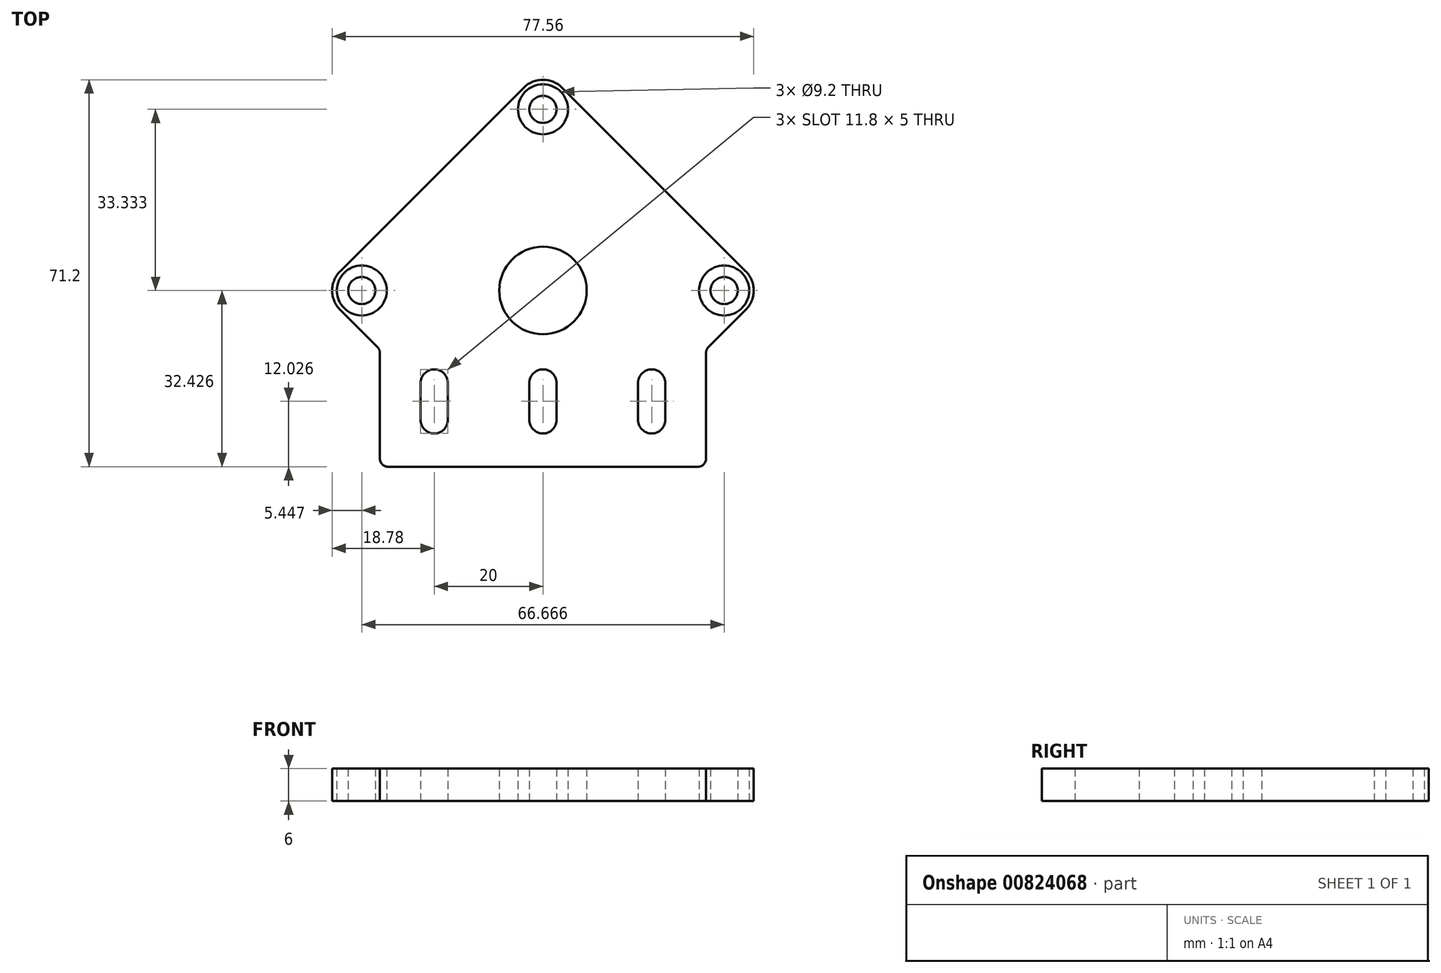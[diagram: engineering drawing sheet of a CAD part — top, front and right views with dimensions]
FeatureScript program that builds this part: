
annotation { "Feature Type Name" : "Feature", "Feature Type Description" : "" }
export const myFeature = defineFeature(function(context is Context, id is Id, definition is map)
    precondition{}
    {
        {
            var Q0;
            Q0=qCreatedBy(makeId("Top.planeOp"),FACE);
            var sketch = newSketch(context, id + "F0", { "sketchPlane" : qUnion([Q0])});
            skLineSegment(sketch, "E0", {"start": v(-28.5, -35.6) * mm, "end": v(28.5, -35.6) * mm});
            skLineSegment(sketch, "E1", {"start": v(-37.31, -6.7) * mm, "end": v(-30.44, -13.58) * mm});
            skLineSegment(sketch, "E2", {"start": v(-30, -14.65) * mm, "end": v(-30, -34.1) * mm});
            skLineSegment(sketch, "E3", {"start": v(-3.54, 34.14) * mm, "end": v(-37.31, 0.36) * mm});
            skLineSegment(sketch, "E4", {"start": v(-22.5, -26.97) * mm, "end": v(-22.5, -20.17) * mm});
            skLineSegment(sketch, "E5", {"start": v(-17.5, -20.17) * mm, "end": v(-17.5, -26.97) * mm});
            skLineSegment(sketch, "E6", {"start": v(-2.5, -26.97) * mm, "end": v(-2.5, -20.17) * mm});
            skLineSegment(sketch, "E7", {"start": v(2.5, -20.17) * mm, "end": v(2.5, -26.97) * mm});
            skLineSegment(sketch, "E8", {"start": v(17.5, -26.97) * mm, "end": v(17.5, -20.17) * mm});
            skLineSegment(sketch, "E9", {"start": v(22.5, -20.17) * mm, "end": v(22.5, -26.97) * mm});
            skLineSegment(sketch, "E10", {"start": v(37.31, 0.36) * mm, "end": v(3.54, 34.14) * mm});
            skLineSegment(sketch, "E11", {"start": v(30, -34.1) * mm, "end": v(30, -14.65) * mm});
            skLineSegment(sketch, "E12", {"start": v(30.44, -13.58) * mm, "end": v(37.31, -6.7) * mm});
            skCircle(sketch, "E13", {"center": v(0, -3.17) * mm, "radius": 8.05 * mm});
            skCircle(sketch, "E14", {"center": v(0, -3.17) * mm, "radius": 5.5 * mm});
            skArc(sketch, "E15", {"start": v(37.31, -6.7) * mm, "mid": v(38.78, -3.17) * mm, "end": v(37.31, 0.36) * mm});
            skArc(sketch, "E16", {"start": v(3.54, 34.14) * mm, "mid": v(0, 35.6) * mm, "end": v(-3.54, 34.14) * mm});
            skArc(sketch, "E17", {"start": v(-37.31, 0.36) * mm, "mid": v(-38.78, -3.17) * mm, "end": v(-37.31, -6.7) * mm});
            skCircle(sketch, "E18", {"center": v(0, 30.16) * mm, "radius": 2.5 * mm});
            skCircle(sketch, "E19", {"center": v(33.33, -3.17) * mm, "radius": 2.5 * mm});
            skCircle(sketch, "E20", {"center": v(-33.33, -3.17) * mm, "radius": 2.5 * mm});
            skArc(sketch, "E21", {"start": v(17.5, -26.97) * mm, "mid": v(20, -29.47) * mm, "end": v(22.5, -26.97) * mm});
            skArc(sketch, "E22", {"start": v(22.5, -20.17) * mm, "mid": v(20, -17.67) * mm, "end": v(17.5, -20.17) * mm});
            skArc(sketch, "E23", {"start": v(-2.5, -26.97) * mm, "mid": v(0, -29.47) * mm, "end": v(2.5, -26.97) * mm});
            skArc(sketch, "E24", {"start": v(2.5, -20.17) * mm, "mid": v(0, -17.67) * mm, "end": v(-2.5, -20.17) * mm});
            skArc(sketch, "E25", {"start": v(-22.5, -26.97) * mm, "mid": v(-20, -29.47) * mm, "end": v(-17.5, -26.97) * mm});
            skArc(sketch, "E26", {"start": v(-17.5, -20.17) * mm, "mid": v(-20, -17.67) * mm, "end": v(-22.5, -20.17) * mm});
            skArc(sketch, "E27", {"start": v(28.5, -35.6) * mm, "mid": v(29.56, -35.16) * mm, "end": v(30, -34.1) * mm});
            skArc(sketch, "E28", {"start": v(30.44, -13.58) * mm, "mid": v(30.11, -14.07) * mm, "end": v(30, -14.65) * mm});
            skArc(sketch, "E29", {"start": v(-30, -14.65) * mm, "mid": v(-30.11, -14.07) * mm, "end": v(-30.44, -13.58) * mm});
            skArc(sketch, "E30", {"start": v(-30, -34.1) * mm, "mid": v(-29.56, -35.16) * mm, "end": v(-28.5, -35.6) * mm});
            skCircle(sketch, "E31.0", {"center": v(-33.33, -3.17) * mm, "radius": 4.6 * mm});
            skArc(sketch, "E32.0", {"start": v(-15.4, -20.17) * mm, "mid": v(-20, -15.57) * mm, "end": v(-24.6, -20.17) * mm});
            skLineSegment(sketch, "E32.1", {"start": v(-15.4, -20.17) * mm, "end": v(-15.4, -26.97) * mm});
            skArc(sketch, "E32.2", {"start": v(-24.6, -26.97) * mm, "mid": v(-20, -31.57) * mm, "end": v(-15.4, -26.97) * mm});
            skLineSegment(sketch, "E32.3", {"start": v(-24.6, -26.97) * mm, "end": v(-24.6, -20.17) * mm});
            skLineSegment(sketch, "E33.0", {"start": v(-4.6, -26.97) * mm, "end": v(-4.6, -20.17) * mm});
            skArc(sketch, "E33.1", {"start": v(-4.6, -26.97) * mm, "mid": v(0, -31.57) * mm, "end": v(4.6, -26.97) * mm});
            skLineSegment(sketch, "E33.2", {"start": v(4.6, -20.17) * mm, "end": v(4.6, -26.97) * mm});
            skArc(sketch, "E33.3", {"start": v(4.6, -20.17) * mm, "mid": v(0, -15.57) * mm, "end": v(-4.6, -20.17) * mm});
            skLineSegment(sketch, "E34.0", {"start": v(15.4, -26.97) * mm, "end": v(15.4, -20.17) * mm});
            skArc(sketch, "E34.1", {"start": v(15.4, -26.97) * mm, "mid": v(20, -31.57) * mm, "end": v(24.6, -26.97) * mm});
            skLineSegment(sketch, "E34.2", {"start": v(24.6, -20.17) * mm, "end": v(24.6, -26.97) * mm});
            skArc(sketch, "E34.3", {"start": v(24.6, -20.17) * mm, "mid": v(20, -15.57) * mm, "end": v(15.4, -20.17) * mm});
            skCircle(sketch, "E35.0", {"center": v(33.33, -3.17) * mm, "radius": 4.6 * mm});
            skCircle(sketch, "E36.0", {"center": v(0, 30.16) * mm, "radius": 4.6 * mm});
            skSolve(sketch);
        }
        {
            var Q0;
            Q0 = qSketchRegion(id + "F0", true);
            var Q1;
            Q1=makeQuery(id+"F0.imprint","IMPRINT",FACE,{"disambiguationData":[TD([[makeQuery(id+"F0.imprint","IMPRINT",EDGE,{"derivedFrom":sQuery(id+"F0.wireOp",EDGE,"E20")}),1.0]])]});
            var Q2;
            Q2=makeQuery(id+"F0.imprint","IMPRINT",FACE,{"disambiguationData":[TD([[makeQuery(id+"F0.imprint","IMPRINT",EDGE,{"derivedFrom":sQuery(id+"F0.wireOp",EDGE,"E18")}),1.0]])]});
            var Q3;
            Q3=makeQuery(id+"F0.imprint","IMPRINT",FACE,{"disambiguationData":[TD([[makeQuery(id+"F0.imprint","IMPRINT",EDGE,{"derivedFrom":sQuery(id+"F0.wireOp",EDGE,"E19")}),1.0]])]});
            var Q4;
            Q4=makeQuery(id+"F0.imprint","IMPRINT",FACE,{"disambiguationData":[TD([[makeQuery(id+"F0.imprint","IMPRINT",EDGE,{"derivedFrom":sQuery(id+"F0.wireOp",EDGE,"E8")}),1.0]])]});
            var Q5;
            Q5=makeQuery(id+"F0.imprint","IMPRINT",FACE,{"disambiguationData":[TD([[makeQuery(id+"F0.imprint","IMPRINT",EDGE,{"derivedFrom":sQuery(id+"F0.wireOp",EDGE,"E6")}),1.0]])]});
            var Q6;
            Q6=makeQuery(id+"F0.imprint","IMPRINT",FACE,{"disambiguationData":[TD([[makeQuery(id+"F0.imprint","IMPRINT",EDGE,{"derivedFrom":sQuery(id+"F0.wireOp",EDGE,"E4")}),1.0]])]});
            extrude(context, id + "F1", {"entities" : qUnion([Q0, Q1, Q2, Q3, Q4, Q5, Q6]), "depth" : 6 * mm, "offsetDistance" : 25 * mm});
        }
    });
